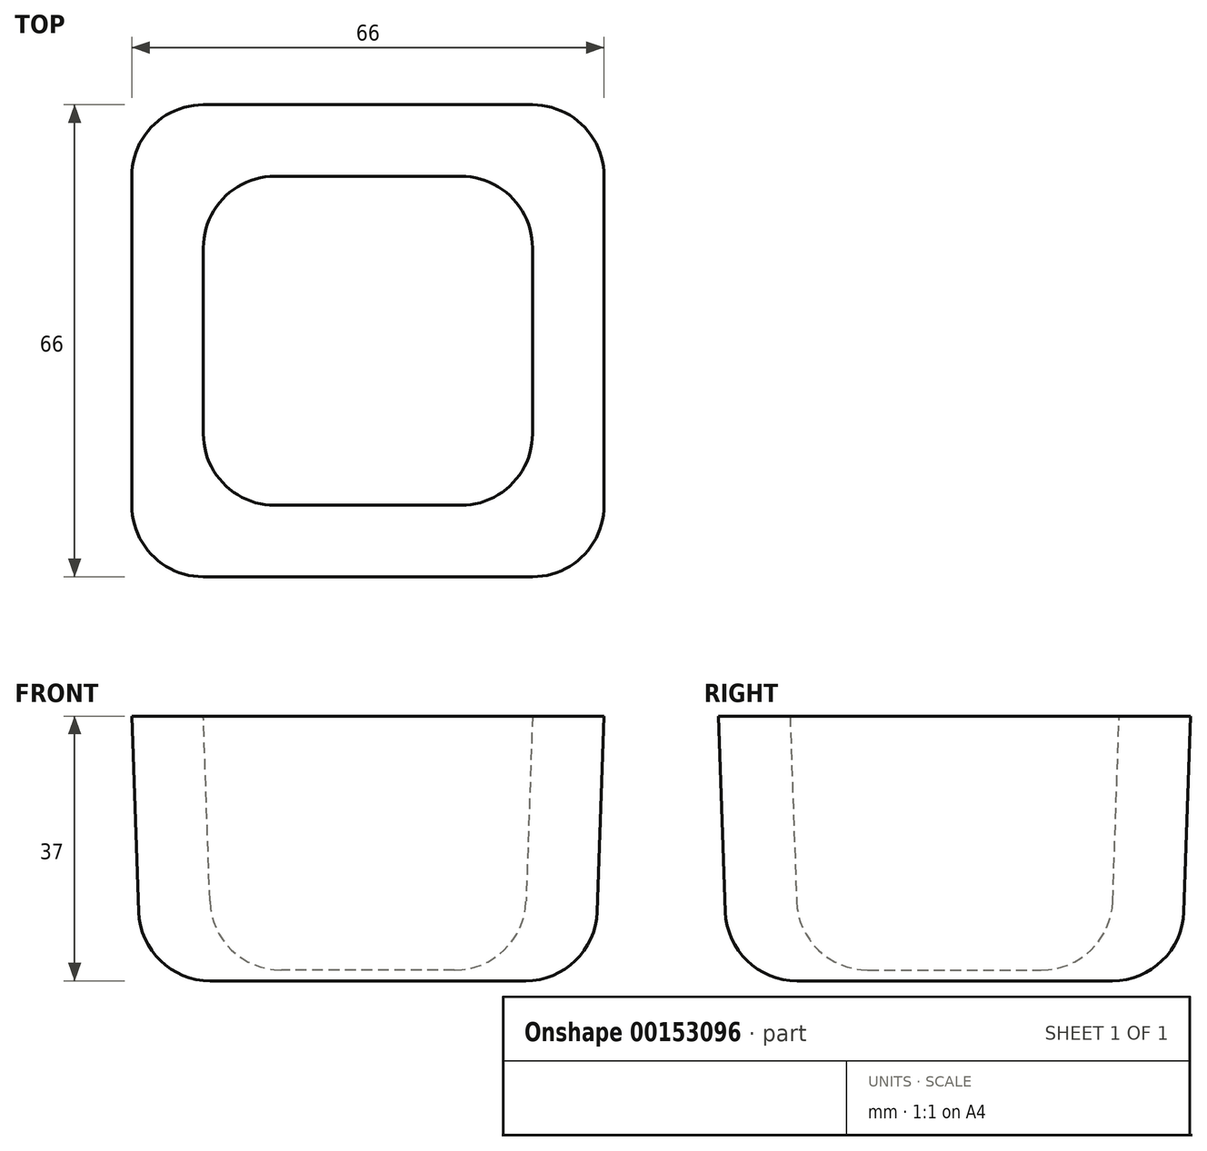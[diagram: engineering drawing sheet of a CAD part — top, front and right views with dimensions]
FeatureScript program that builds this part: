
annotation { "Feature Type Name" : "Feature", "Feature Type Description" : "" }
export const myFeature = defineFeature(function(context is Context, id is Id, definition is map)
    precondition{}
    {
        {
            var Q0;
            Q0=qCreatedBy(makeId("Top.planeOp"),FACE);
            var sketch = newSketch(context, id + "F0", { "sketchPlane" : qUnion([Q0])});
            skLineSegment(sketch, "E0.bottom", {"start": v(0, 0) * mm, "end": v(66, 0) * mm});
            skLineSegment(sketch, "E0.top", {"start": v(0, 66) * mm, "end": v(66, 66) * mm});
            skLineSegment(sketch, "E0.left", {"start": v(0, 0) * mm, "end": v(0, 66) * mm});
            skLineSegment(sketch, "E0.right", {"start": v(66, 0) * mm, "end": v(66, 66) * mm});
            skLineSegment(sketch, "E1.bottom", {"start": v(10, 10) * mm, "end": v(56, 10) * mm});
            skLineSegment(sketch, "E1.top", {"start": v(10, 56) * mm, "end": v(56, 56) * mm});
            skLineSegment(sketch, "E1.left", {"start": v(10, 10) * mm, "end": v(10, 56) * mm});
            skLineSegment(sketch, "E1.right", {"start": v(56, 10) * mm, "end": v(56, 56) * mm});
            skSolve(sketch);
        }
        {
            var Q0;
            Q0=makeQuery(id+"F0.imprint","IMPRINT",FACE,{"disambiguationData":[TD([[makeQuery(id+"F0.imprint","IMPRINT",EDGE,{"derivedFrom":sQuery(id+"F0.wireOp",EDGE,"E0.bottom")}),1.0]])]});
            var Q1;
            Q1=makeQuery(id+"F0.imprint","IMPRINT",FACE,{"disambiguationData":[TD([[makeQuery(id+"F0.imprint","IMPRINT",EDGE,{"derivedFrom":sQuery(id+"F0.wireOp",EDGE,"E1.bottom")}),1.0]])]});
            extrude(context, id + "F1", {"entities" : qUnion([Q0, Q1]), "oppositeDirection" : true, "depth" : 37 * mm, "hasDraft" : true, "draftAngle" : 2 * degree, "draftPullDirection" : true});
        }
        {
            var Q0;
            Q0=makeQuery(id+"F0.imprint","IMPRINT",FACE,{"disambiguationData":[TD([[makeQuery(id+"F0.imprint","IMPRINT",EDGE,{"derivedFrom":sQuery(id+"F0.wireOp",EDGE,"E1.bottom")}),1.0]])]});
            extrude(context, id + "F2", {"entities" : qUnion([Q0]), "operationType" : NewBodyOperationType.REMOVE, "oppositeDirection" : true, "depth" : 35.5 * mm, "hasDraft" : true, "draftAngle" : 2 * degree, "draftPullDirection" : true});
        }
        {
            var Q0;
            Q0=makeQuery(id+"F2.boolean.opBoolean","COPY",FACE,{"derivedFrom":makeQuery(id+"F2.opExtrude","CAP_FACE",FACE,{"disambiguationData":[OSD([sQuery(id+"F0.wireOp",EDGE,"E1.bottom"),sQuery(id+"F0.wireOp",EDGE,"E1.top"),sQuery(id+"F0.wireOp",EDGE,"E1.left"),sQuery(id+"F0.wireOp",EDGE,"E1.right")])],"isStart":false})});
            var Q1;
            Q1=makeQuery(id+"F2.boolean.opBoolean","COPY",EDGE,{"derivedFrom":makeQuery(id+"F2.opExtrude","SWEPT_EDGE",EDGE,{"disambiguationData":[OSD([sQuery(id+"F0.wireOp",EDGE,"E1.bottom"),sQuery(id+"F0.wireOp",EDGE,"E1.right")])]})});
            var Q2;
            Q2=makeQuery(id+"F2.boolean.opBoolean","COPY",EDGE,{"derivedFrom":makeQuery(id+"F2.opExtrude","SWEPT_EDGE",EDGE,{"disambiguationData":[OSD([sQuery(id+"F0.wireOp",EDGE,"E1.top"),sQuery(id+"F0.wireOp",EDGE,"E1.left")])]})});
            var Q3;
            Q3=makeQuery(id+"F2.boolean.opBoolean","COPY",EDGE,{"derivedFrom":makeQuery(id+"F2.opExtrude","SWEPT_EDGE",EDGE,{"disambiguationData":[OSD([sQuery(id+"F0.wireOp",EDGE,"E1.bottom"),sQuery(id+"F0.wireOp",EDGE,"E1.left")])]})});
            var Q4;
            Q4=makeQuery(id+"F2.boolean.opBoolean","COPY",EDGE,{"derivedFrom":makeQuery(id+"F2.opExtrude","SWEPT_EDGE",EDGE,{"disambiguationData":[OSD([sQuery(id+"F0.wireOp",EDGE,"E1.top"),sQuery(id+"F0.wireOp",EDGE,"E1.right")])]})});
            fillet(context, id + "F3", {"entities" : qUnion([Q0, Q1, Q2, Q3, Q4]), "radius" : 10 * mm, "tangentPropagation" : true, "allowEdgeOverflow" : false});
        }
        {
            var Q0;
            Q0=makeQuery(id+"F1.opExtrude","CAP_FACE",FACE,{"disambiguationData":[OSD([sQuery(id+"F0.wireOp",EDGE,"E0.bottom"),sQuery(id+"F0.wireOp",EDGE,"E0.top"),sQuery(id+"F0.wireOp",EDGE,"E0.left"),sQuery(id+"F0.wireOp",EDGE,"E0.right")])],"isStart":false});
            var Q1;
            Q1=makeQuery(id+"F1.opExtrude","SWEPT_EDGE",EDGE,{"disambiguationData":[OSD([sQuery(id+"F0.wireOp",EDGE,"E0.top"),sQuery(id+"F0.wireOp",EDGE,"E0.right")])]});
            var Q2;
            Q2=makeQuery(id+"F1.opExtrude","SWEPT_EDGE",EDGE,{"disambiguationData":[OSD([sQuery(id+"F0.wireOp",EDGE,"E0.top"),sQuery(id+"F0.wireOp",EDGE,"E0.left")])]});
            var Q3;
            Q3=makeQuery(id+"F1.opExtrude","SWEPT_EDGE",EDGE,{"disambiguationData":[OSD([sQuery(id+"F0.wireOp",EDGE,"E0.bottom"),sQuery(id+"F0.wireOp",EDGE,"E0.left")])]});
            var Q4;
            Q4=makeQuery(id+"F1.opExtrude","SWEPT_EDGE",EDGE,{"disambiguationData":[OSD([sQuery(id+"F0.wireOp",EDGE,"E0.bottom"),sQuery(id+"F0.wireOp",EDGE,"E0.right")])]});
            fillet(context, id + "F4", {"entities" : qUnion([Q0, Q1, Q2, Q3, Q4]), "radius" : 10 * mm, "tangentPropagation" : true, "allowEdgeOverflow" : false});
        }
    });
